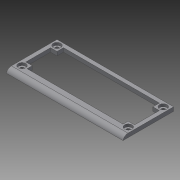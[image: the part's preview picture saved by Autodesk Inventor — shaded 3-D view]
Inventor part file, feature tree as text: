
AUTODESK INVENTOR PART (.ipt)
format: ipt  version: 2015 (Build 190159000, 159)  size: 185,856 bytes
history: native  units: mm
features: extrude x10, sketch x10, other x1, fillet x1
ambient origin geometry x8: Origin, YZ Plane, XZ Plane, XY Plane, X Axis, Y Axis, Z Axis, Center Point
bodies: Body1 (feature_tree), Body2 (feature_tree)
feature tree (22):
  other  "ソリッド1"
  extrude  "押し出し1"  Depth=90.0mm
  extrude  "押し出し2"  Depth=7.0mm
  extrude  "押し出し3"  Depth=3.0mm TaperAngle=0.0deg
  extrude  "押し出し4"  Depth=5.8mm
  fillet  "フィレット1"  Radius=5.8mm
  extrude  "押し出し5"  Depth=3.9mm
  extrude  "押し出し6"  Depth=3.9mm
  extrude  "押し出し7"  Depth=82.0mm
  extrude  "押し出し8"  Depth=4.0mm
  extrude  "押し出し9"  Depth=2.0mm TaperAngle=0.0deg
  extrude  "押し出し10"  Depth=3.0mm
  sketch  "スケッチ1"
  sketch  "スケッチ2"
  sketch  "スケッチ3"
  sketch  "スケッチ4"
  sketch  "スケッチ6"
  sketch  "スケッチ7"
  sketch  "スケッチ8"
  sketch  "スケッチ9"
  sketch  "スケッチ10"
  sketch  "スケッチ11"
